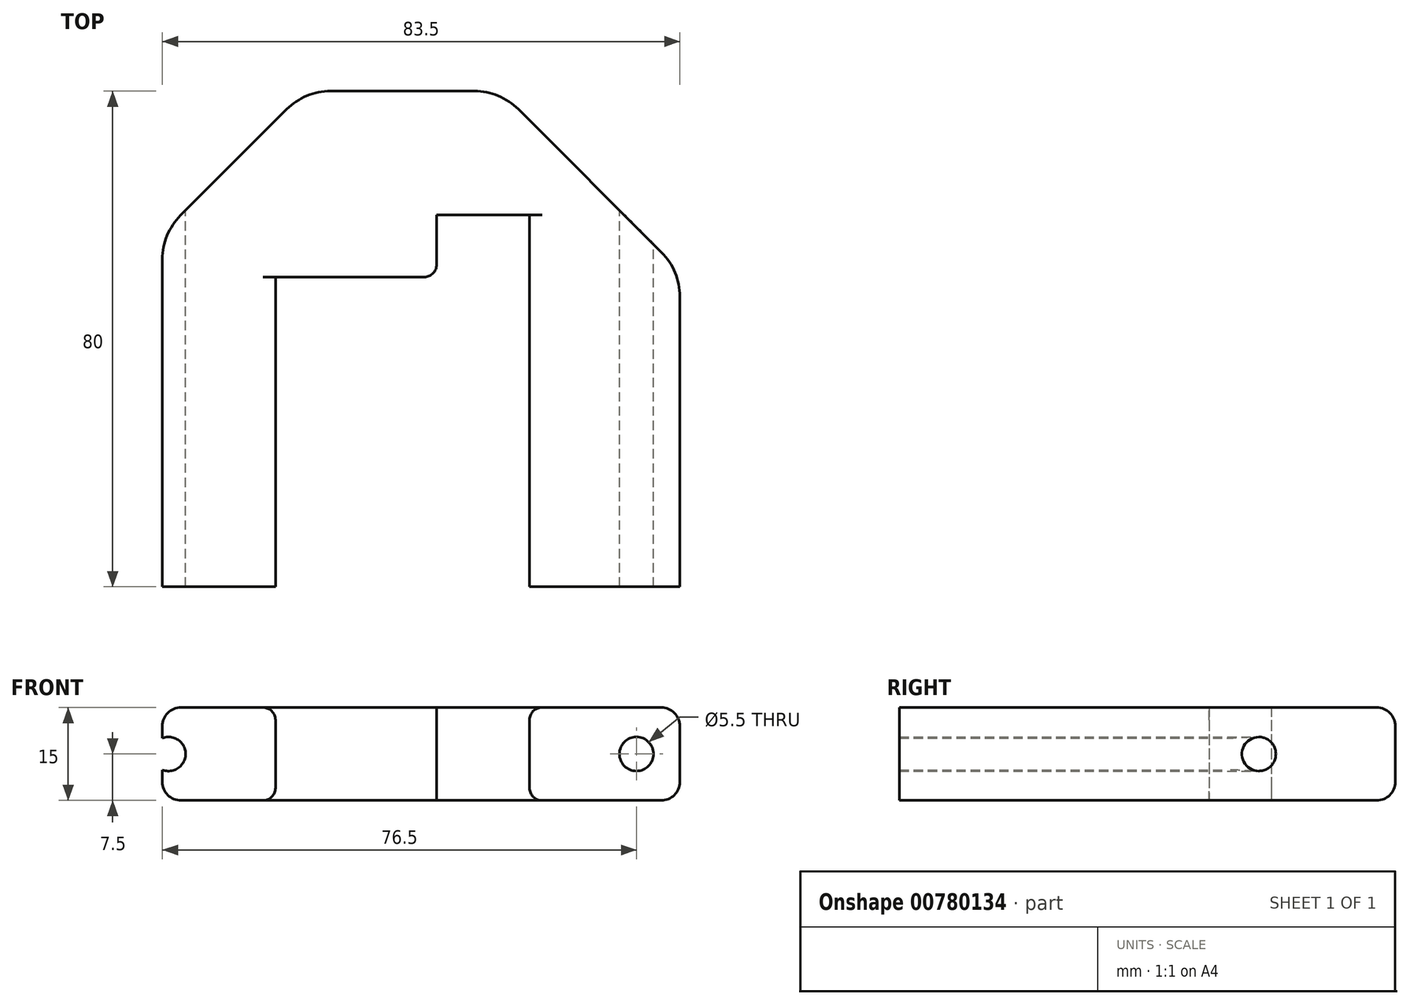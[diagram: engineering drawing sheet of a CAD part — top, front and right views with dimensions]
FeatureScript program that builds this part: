
annotation { "Feature Type Name" : "Feature", "Feature Type Description" : "" }
export const myFeature = defineFeature(function(context is Context, id is Id, definition is map)
    precondition{}
    {
        {
            var Q0;
            Q0=qCreatedBy(makeId("Front.planeOp"),FACE);
            var sketch = newSketch(context, id + "F0", { "sketchPlane" : qUnion([Q0])});
            skLineSegment(sketch, "E0.bottom", {"start": v(-38.75, 15) * mm, "end": v(-20.5, 15) * mm});
            skLineSegment(sketch, "E0.top", {"start": v(-38.75, 0) * mm, "end": v(-20.5, 0) * mm});
            skLineSegment(sketch, "E0.left", {"start": v(-38.75, 15) * mm, "end": v(-38.75, 0) * mm});
            skLineSegment(sketch, "E0.right", {"start": v(-20.5, 15) * mm, "end": v(-20.5, 0) * mm});
            skLineSegment(sketch, "E1", {"start": v(-38.75, 7.5) * mm, "end": v(-37.75, 7.5) * mm});
            skCircle(sketch, "E2", {"center": v(-37.75, 7.5) * mm, "radius": 2.75 * mm});
            skLineSegment(sketch, "E3", {"start": v(0, 35.3) * mm, "end": v(0, -13.85) * mm});
            skLineSegment(sketch, "E4.MirrorCS", {"start": v(38.75, 0) * mm, "end": v(20.5, 0) * mm});
            skLineSegment(sketch, "E5.MirrorCS", {"start": v(38.75, 15) * mm, "end": v(20.5, 15) * mm});
            skLineSegment(sketch, "E6.MirrorCS", {"start": v(38.75, 15) * mm, "end": v(38.75, 0) * mm});
            skCircle(sketch, "E7.MirrorC", {"center": v(37.75, 7.5) * mm, "radius": 2.75 * mm});
            skLineSegment(sketch, "E8.MirrorCS", {"start": v(20.5, 15) * mm, "end": v(20.5, 0) * mm});
            skLineSegment(sketch, "E9.bottom", {"start": v(20.5, 15) * mm, "end": v(5.5, 15) * mm});
            skLineSegment(sketch, "E9.top", {"start": v(20.5, 0) * mm, "end": v(5.5, 0) * mm});
            skLineSegment(sketch, "E9.right", {"start": v(5.5, 15) * mm, "end": v(5.5, 0) * mm});
            skLineSegment(sketch, "E10.bottom", {"start": v(-20.5, 15) * mm, "end": v(5.5, 15) * mm});
            skLineSegment(sketch, "E10.top", {"start": v(-20.5, 15) * mm, "end": v(5.5, 15) * mm});
            skLineSegment(sketch, "E10.left", {"start": v(-20.5, 15) * mm, "end": v(-20.5, 15) * mm});
            skLineSegment(sketch, "E10.right", {"start": v(5.5, 15) * mm, "end": v(5.5, 15) * mm});
            skLineSegment(sketch, "E11.bottom", {"start": v(5.5, 0) * mm, "end": v(-20.5, 0) * mm});
            skLineSegment(sketch, "E11.top", {"start": v(5.5, 0) * mm, "end": v(-20.5, 0) * mm});
            skLineSegment(sketch, "E11.left", {"start": v(5.5, 0) * mm, "end": v(5.5, 0) * mm});
            skLineSegment(sketch, "E11.right", {"start": v(-20.5, 0) * mm, "end": v(-20.5, 0) * mm});
            skLineSegment(sketch, "E12.bottom", {"start": v(38.75, 0) * mm, "end": v(44.75, 0) * mm});
            skLineSegment(sketch, "E12.top", {"start": v(38.75, 15) * mm, "end": v(44.75, 15) * mm});
            skLineSegment(sketch, "E12.left", {"start": v(38.75, 0) * mm, "end": v(38.75, 15) * mm});
            skLineSegment(sketch, "E12.right", {"start": v(44.75, 0) * mm, "end": v(44.75, 15) * mm});
            skSolve(sketch);
        }
        {
            var Q0;
            {var subQ1=sQuery(id+"F0.wireOp",EDGE,"E0.bottom");Q0=makeQuery(id+"F0.imprint","IMPRINT",FACE,{"disambiguationData":[TD([[makeQuery(id+"F0.imprint","IMPRINT",EDGE,{"derivedFrom":subQ1}),-1.0]])]});}
            var Q1;
            {var subQ1=sQuery(id+"F0.wireOp",EDGE,"E4.MirrorCS");Q1=makeQuery(id+"F0.imprint","IMPRINT",FACE,{"disambiguationData":[TD([[makeQuery(id+"F0.imprint","IMPRINT",EDGE,{"derivedFrom":subQ1}),-1.0]])]});}
            var Q2;
            {var subQ1=sQuery(id+"F0.wireOp",EDGE,"E12.bottom");Q2=makeQuery(id+"F0.imprint","IMPRINT",FACE,{"disambiguationData":[TD([[makeQuery(id+"F0.imprint","IMPRINT",EDGE,{"derivedFrom":subQ1}),1.0]])]});}
            extrude(context, id + "F1", {"entities" : qUnion([Q0, Q1, Q2]), "depth" : 80 * mm, "offsetDistance" : 25 * mm});
        }
        {
            var Q0;
            {var subQ0=sQuery(id+"F0.wireOp",EDGE,"E0.right");Q0=makeQuery(id+"F0.imprint","IMPRINT",FACE,{"disambiguationData":[TD([[makeQuery(id+"F0.imprint","IMPRINT",EDGE,{"derivedFrom":subQ0}),1.0]])]});}
            var Q1;
            {var subQ5=sQuery(id+"F0.wireOp",EDGE,"E9.right");Q1=makeQuery(id+"F0.imprint","IMPRINT",FACE,{"disambiguationData":[TD([[makeQuery(id+"F0.imprint","IMPRINT",EDGE,{"derivedFrom":subQ5}),-1.0]])]});}
            extrude(context, id + "F2", {"entities" : qUnion([Q0, Q1]), "operationType" : NewBodyOperationType.ADD, "depth" : 30 * mm, "offsetDistance" : 25 * mm});
        }
        {
            var Q0;
            Q0=makeQuery(id+"F0.imprint","IMPRINT",FACE,{"disambiguationData":[TD([[makeQuery(id+"F0.imprint","IMPRINT",EDGE,{"derivedFrom":sQuery(id+"F0.wireOp",EDGE,"E9.bottom")}),1.0]])]});
            extrude(context, id + "F3", {"entities" : qUnion([Q0]), "operationType" : NewBodyOperationType.ADD, "depth" : 20 * mm, "offsetDistance" : 25 * mm});
        }
        {
            var Q0;
            {var subQ0=sQuery(id+"F0.wireOp",EDGE,"E0.left");Q0=makeQuery(id+"F1.opExtrude","CAP_EDGE",EDGE,{"disambiguationData":[OSD([subQ0]),TDD([makeQuery(id+"F0.imprint","IMPRINT",EDGE,{"disambiguationData":[TD([[makeQuery(id+"F0.imprint","INTERSECT",VERTEX,{"derivedFrom":[sQuery(id+"F0.wireOp",EDGE,"E0.top"),subQ0]}),1.0]])],"derivedFrom":subQ0})])],"isStart":true});}
            var Q1;
            {var subQ0=sQuery(id+"F0.wireOp",EDGE,"E0.left");Q1=makeQuery(id+"F1.opExtrude","CAP_EDGE",EDGE,{"disambiguationData":[OSD([subQ0]),TDD([makeQuery(id+"F0.imprint","IMPRINT",EDGE,{"disambiguationData":[TD([[makeQuery(id+"F0.imprint","INTERSECT",VERTEX,{"derivedFrom":[sQuery(id+"F0.wireOp",EDGE,"E0.bottom"),subQ0]}),-1.0]])],"derivedFrom":subQ0})])],"isStart":true});}
            var Q2;
            {var subQ0=sQuery(id+"F0.wireOp",EDGE,"E6.MirrorCS");Q2=makeQuery(id+"F1.opExtrude","CAP_EDGE",EDGE,{"disambiguationData":[OSD([subQ0]),TDD([makeQuery(id+"F0.imprint","IMPRINT",EDGE,{"disambiguationData":[TD([[makeQuery(id+"F0.imprint","INTERSECT",VERTEX,{"derivedFrom":[sQuery(id+"F0.wireOp",EDGE,"E4.MirrorCS"),subQ0]}),1.0]])],"derivedFrom":subQ0})])],"isStart":true});}
            var Q3;
            {var subQ0=sQuery(id+"F0.wireOp",EDGE,"E6.MirrorCS");Q3=makeQuery(id+"F1.opExtrude","CAP_EDGE",EDGE,{"disambiguationData":[OSD([subQ0]),TDD([makeQuery(id+"F0.imprint","IMPRINT",EDGE,{"disambiguationData":[TD([[makeQuery(id+"F0.imprint","INTERSECT",VERTEX,{"derivedFrom":[sQuery(id+"F0.wireOp",EDGE,"E5.MirrorCS"),subQ0]}),-1.0]])],"derivedFrom":subQ0})])],"isStart":true});}
            chamfer(context, id + "F4", {"entities" : qUnion([Q0, Q1, Q2, Q3]), "width" : 23 * mm, "tangentPropagation" : true});
        }
        {
            var Q0;
            Q0=makeQuery(id+"F1.opExtrude","CAP_EDGE",EDGE,{"disambiguationData":[OSD([sQuery(id+"F0.wireOp",EDGE,"E12.right")])],"isStart":true});
            chamfer(context, id + "F5", {"entities" : qUnion([Q0]), "width" : 29 * mm, "tangentPropagation" : true});
        }
        {
            var Q0;
            {var subQ0=sQuery(id+"F0.wireOp",EDGE,"E9.right");var subQ1=sQuery(id+"F0.wireOp",EDGE,"E8.MirrorCS");var subQ2=sQuery(id+"F0.wireOp",EDGE,"E0.right");var subQ3=sQuery(id+"F0.wireOp",EDGE,"E12.right");Q0=makeQuery(id+"F5.opChamfer","BLEND_EDGE",EDGE,{"blendedFrom":[makeQuery(id+"F1.opExtrude","CAP_EDGE",EDGE,{"disambiguationData":[OSD([subQ3])],"isStart":true}),makeQuery(id+"F3.boolean.opBoolean","MERGE",FACE,{"derivedFrom":[makeQuery(id+"F1.opExtrude","CAP_FACE",FACE,{"disambiguationData":[OSD([sQuery(id+"F0.wireOp",EDGE,"E4.MirrorCS"),sQuery(id+"F0.wireOp",EDGE,"E5.MirrorCS"),sQuery(id+"F0.wireOp",EDGE,"E7.MirrorC"),subQ1,sQuery(id+"F0.wireOp",EDGE,"E12.bottom"),sQuery(id+"F0.wireOp",EDGE,"E12.top"),subQ3])],"isStart":true}),makeQuery(id+"F2.boolean.opBoolean","MERGE",FACE,{"derivedFrom":[makeQuery(id+"F1.opExtrude","CAP_FACE",FACE,{"disambiguationData":[OSD([sQuery(id+"F0.wireOp",EDGE,"E0.bottom"),sQuery(id+"F0.wireOp",EDGE,"E0.top"),sQuery(id+"F0.wireOp",EDGE,"E0.left"),subQ2,sQuery(id+"F0.wireOp",EDGE,"E2")])],"isStart":true}),makeQuery(id+"F2.opExtrude","CAP_FACE",FACE,{"disambiguationData":[OSD([subQ2,subQ0,sQuery(id+"F0.wireOp",EDGE,"E10.top"),sQuery(id+"F0.wireOp",EDGE,"E11.top")])],"isStart":true})]}),makeQuery(id+"F3.opExtrude","CAP_FACE",FACE,{"disambiguationData":[OSD([sQuery(id+"F0.wireOp",EDGE,"E9.bottom"),sQuery(id+"F0.wireOp",EDGE,"E9.top"),subQ1,subQ0])],"isStart":true})]})],"blendedInto":[makeQuery(id+"F3.boolean.opBoolean","MERGE",FACE,{"derivedFrom":[makeQuery(id+"F1.opExtrude","CAP_FACE",FACE,{"disambiguationData":[OSD([sQuery(id+"F0.wireOp",EDGE,"E4.MirrorCS"),sQuery(id+"F0.wireOp",EDGE,"E5.MirrorCS"),sQuery(id+"F0.wireOp",EDGE,"E7.MirrorC"),subQ1,sQuery(id+"F0.wireOp",EDGE,"E12.bottom"),sQuery(id+"F0.wireOp",EDGE,"E12.top"),subQ3])],"isStart":true}),makeQuery(id+"F2.boolean.opBoolean","MERGE",FACE,{"derivedFrom":[makeQuery(id+"F1.opExtrude","CAP_FACE",FACE,{"disambiguationData":[OSD([sQuery(id+"F0.wireOp",EDGE,"E0.bottom"),sQuery(id+"F0.wireOp",EDGE,"E0.top"),sQuery(id+"F0.wireOp",EDGE,"E0.left"),subQ2,sQuery(id+"F0.wireOp",EDGE,"E2")])],"isStart":true}),makeQuery(id+"F2.opExtrude","CAP_FACE",FACE,{"disambiguationData":[OSD([subQ2,subQ0,sQuery(id+"F0.wireOp",EDGE,"E10.top"),sQuery(id+"F0.wireOp",EDGE,"E11.top")])],"isStart":true})]}),makeQuery(id+"F3.opExtrude","CAP_FACE",FACE,{"disambiguationData":[OSD([sQuery(id+"F0.wireOp",EDGE,"E9.bottom"),sQuery(id+"F0.wireOp",EDGE,"E9.top"),subQ1,subQ0])],"isStart":true})]})]});}
            var Q1;
            {var subQ0=sQuery(id+"F0.wireOp",EDGE,"E9.right");var subQ1=sQuery(id+"F0.wireOp",EDGE,"E8.MirrorCS");var subQ2=sQuery(id+"F0.wireOp",EDGE,"E0.right");var subQ3=sQuery(id+"F0.wireOp",EDGE,"E2");var subQ4=sQuery(id+"F0.wireOp",EDGE,"E0.left");var subQ5=sQuery(id+"F0.wireOp",EDGE,"E0.top");Q1=makeQuery(id+"F4.opChamfer","BLEND_EDGE",EDGE,{"blendedFrom":[makeQuery(id+"F1.opExtrude","CAP_EDGE",EDGE,{"disambiguationData":[OSD([subQ4]),TDD([makeQuery(id+"F0.imprint","IMPRINT",EDGE,{"disambiguationData":[TD([[makeQuery(id+"F0.imprint","INTERSECT",VERTEX,{"derivedFrom":[subQ5,subQ4]}),1.0]])],"derivedFrom":subQ4})])],"isStart":true}),makeQuery(id+"F3.boolean.opBoolean","MERGE",FACE,{"derivedFrom":[makeQuery(id+"F1.opExtrude","CAP_FACE",FACE,{"disambiguationData":[OSD([sQuery(id+"F0.wireOp",EDGE,"E4.MirrorCS"),sQuery(id+"F0.wireOp",EDGE,"E5.MirrorCS"),sQuery(id+"F0.wireOp",EDGE,"E7.MirrorC"),subQ1,sQuery(id+"F0.wireOp",EDGE,"E12.bottom"),sQuery(id+"F0.wireOp",EDGE,"E12.top"),sQuery(id+"F0.wireOp",EDGE,"E12.right")])],"isStart":true}),makeQuery(id+"F2.boolean.opBoolean","MERGE",FACE,{"derivedFrom":[makeQuery(id+"F1.opExtrude","CAP_FACE",FACE,{"disambiguationData":[OSD([sQuery(id+"F0.wireOp",EDGE,"E0.bottom"),subQ5,subQ4,subQ2,subQ3])],"isStart":true}),makeQuery(id+"F2.opExtrude","CAP_FACE",FACE,{"disambiguationData":[OSD([subQ2,subQ0,sQuery(id+"F0.wireOp",EDGE,"E10.top"),sQuery(id+"F0.wireOp",EDGE,"E11.top")])],"isStart":true})]}),makeQuery(id+"F3.opExtrude","CAP_FACE",FACE,{"disambiguationData":[OSD([sQuery(id+"F0.wireOp",EDGE,"E9.bottom"),sQuery(id+"F0.wireOp",EDGE,"E9.top"),subQ1,subQ0])],"isStart":true})]})],"blendedInto":[makeQuery(id+"F3.boolean.opBoolean","MERGE",FACE,{"derivedFrom":[makeQuery(id+"F1.opExtrude","CAP_FACE",FACE,{"disambiguationData":[OSD([sQuery(id+"F0.wireOp",EDGE,"E4.MirrorCS"),sQuery(id+"F0.wireOp",EDGE,"E5.MirrorCS"),sQuery(id+"F0.wireOp",EDGE,"E7.MirrorC"),subQ1,sQuery(id+"F0.wireOp",EDGE,"E12.bottom"),sQuery(id+"F0.wireOp",EDGE,"E12.top"),sQuery(id+"F0.wireOp",EDGE,"E12.right")])],"isStart":true}),makeQuery(id+"F2.boolean.opBoolean","MERGE",FACE,{"derivedFrom":[makeQuery(id+"F1.opExtrude","CAP_FACE",FACE,{"disambiguationData":[OSD([sQuery(id+"F0.wireOp",EDGE,"E0.bottom"),subQ5,subQ4,subQ2,subQ3])],"isStart":true}),makeQuery(id+"F2.opExtrude","CAP_FACE",FACE,{"disambiguationData":[OSD([subQ2,subQ0,sQuery(id+"F0.wireOp",EDGE,"E10.top"),sQuery(id+"F0.wireOp",EDGE,"E11.top")])],"isStart":true})]}),makeQuery(id+"F3.opExtrude","CAP_FACE",FACE,{"disambiguationData":[OSD([sQuery(id+"F0.wireOp",EDGE,"E9.bottom"),sQuery(id+"F0.wireOp",EDGE,"E9.top"),subQ1,subQ0])],"isStart":true})]})]});}
            var Q2;
            {var subQ0=sQuery(id+"F0.wireOp",EDGE,"E12.right");Q2=makeQuery(id+"F5.opChamfer","BLEND_EDGE",EDGE,{"blendedFrom":[makeQuery(id+"F1.opExtrude","CAP_EDGE",EDGE,{"disambiguationData":[OSD([subQ0])],"isStart":true}),makeQuery(id+"F1.opExtrude","SWEPT_FACE",FACE,{"disambiguationData":[OSD([subQ0])]})],"blendedInto":[makeQuery(id+"F1.opExtrude","SWEPT_FACE",FACE,{"disambiguationData":[OSD([subQ0])]})]});}
            var Q3;
            {var subQ0=sQuery(id+"F0.wireOp",EDGE,"E0.left");var subQ1=makeQuery(id+"F0.imprint","IMPRINT",EDGE,{"disambiguationData":[TD([[makeQuery(id+"F0.imprint","INTERSECT",VERTEX,{"derivedFrom":[sQuery(id+"F0.wireOp",EDGE,"E0.top"),subQ0]}),1.0]])],"derivedFrom":subQ0});Q3=makeQuery(id+"F4.opChamfer","BLEND_EDGE",EDGE,{"blendedFrom":[makeQuery(id+"F1.opExtrude","CAP_EDGE",EDGE,{"disambiguationData":[OSD([subQ0]),TDD([subQ1])],"isStart":true}),makeQuery(id+"F1.opExtrude","SWEPT_FACE",FACE,{"disambiguationData":[OSD([subQ0]),TDD([subQ1])]})],"blendedInto":[makeQuery(id+"F1.opExtrude","SWEPT_FACE",FACE,{"disambiguationData":[OSD([subQ0]),TDD([subQ1])]})]});}
            var Q4;
            {var subQ0=sQuery(id+"F0.wireOp",EDGE,"E0.left");Q4=makeQuery(id+"F4.opChamfer","BLEND_EDGE",EDGE,{"blendedFrom":[makeQuery(id+"F1.opExtrude","CAP_EDGE",EDGE,{"disambiguationData":[OSD([subQ0]),TDD([makeQuery(id+"F0.imprint","IMPRINT",EDGE,{"disambiguationData":[TD([[makeQuery(id+"F0.imprint","INTERSECT",VERTEX,{"derivedFrom":[sQuery(id+"F0.wireOp",EDGE,"E0.top"),subQ0]}),1.0]])],"derivedFrom":subQ0})])],"isStart":true}),makeQuery(id+"F1.opExtrude","SWEPT_FACE",FACE,{"disambiguationData":[OSD([subQ0]),TDD([makeQuery(id+"F0.imprint","IMPRINT",EDGE,{"disambiguationData":[TD([[makeQuery(id+"F0.imprint","INTERSECT",VERTEX,{"derivedFrom":[sQuery(id+"F0.wireOp",EDGE,"E0.bottom"),subQ0]}),-1.0]])],"derivedFrom":subQ0})])]})],"blendedInto":[makeQuery(id+"F1.opExtrude","SWEPT_FACE",FACE,{"disambiguationData":[OSD([subQ0]),TDD([makeQuery(id+"F0.imprint","IMPRINT",EDGE,{"disambiguationData":[TD([[makeQuery(id+"F0.imprint","INTERSECT",VERTEX,{"derivedFrom":[sQuery(id+"F0.wireOp",EDGE,"E0.bottom"),subQ0]}),-1.0]])],"derivedFrom":subQ0})])]})]});}
            fillet(context, id + "F6", {"entities" : qUnion([Q0, Q1, Q2, Q3, Q4]), "radius" : 10 * mm, "tangentPropagation" : true, "allowEdgeOverflow" : false});
        }
        {
            var Q0;
            Q0=makeQuery(id+"F1.opExtrude","SWEPT_EDGE",EDGE,{"disambiguationData":[OSD([sQuery(id+"F0.wireOp",EDGE,"E5.MirrorCS"),sQuery(id+"F0.wireOp",EDGE,"E9.bottom"),sQuery(id+"F0.wireOp",EDGE,"E8.MirrorCS")])]});
            var Q1;
            Q1=makeQuery(id+"F1.opExtrude","SWEPT_EDGE",EDGE,{"disambiguationData":[OSD([sQuery(id+"F0.wireOp",EDGE,"E4.MirrorCS"),sQuery(id+"F0.wireOp",EDGE,"E9.top"),sQuery(id+"F0.wireOp",EDGE,"E8.MirrorCS")])]});
            var Q2;
            Q2=makeQuery(id+"F1.opExtrude","SWEPT_EDGE",EDGE,{"disambiguationData":[OSD([sQuery(id+"F0.wireOp",EDGE,"E0.bottom"),sQuery(id+"F0.wireOp",EDGE,"E0.right"),sQuery(id+"F0.wireOp",EDGE,"E10.top")])]});
            var Q3;
            Q3=makeQuery(id+"F1.opExtrude","SWEPT_EDGE",EDGE,{"disambiguationData":[OSD([sQuery(id+"F0.wireOp",EDGE,"E0.top"),sQuery(id+"F0.wireOp",EDGE,"E0.right"),sQuery(id+"F0.wireOp",EDGE,"E11.top")])]});
            var Q4;
            Q4=makeQuery(id+"F2.opExtrude","CAP_EDGE",EDGE,{"disambiguationData":[OSD([sQuery(id+"F0.wireOp",EDGE,"E9.right")])],"isStart":false});
            fillet(context, id + "F7", {"entities" : qUnion([Q0, Q1, Q2, Q3, Q4]), "radius" : 2 * mm, "tangentPropagation" : true, "allowEdgeOverflow" : false});
        }
        {
            var Q0;
            Q0=makeQuery(id+"F1.opExtrude","SWEPT_EDGE",EDGE,{"disambiguationData":[OSD([sQuery(id+"F0.wireOp",EDGE,"E0.bottom"),sQuery(id+"F0.wireOp",EDGE,"E0.left")])]});
            var Q1;
            {var subQ0=sQuery(id+"F0.wireOp",EDGE,"E0.bottom");var subQ1=sQuery(id+"F0.wireOp",EDGE,"E0.left");Q1=makeQuery(id+"F6.opFillet","BLEND_EDGE",EDGE,{"blendedFrom":[makeQuery(id+"F4.opChamfer","BLEND_EDGE",EDGE,{"blendedFrom":[makeQuery(id+"F1.opExtrude","CAP_EDGE",EDGE,{"disambiguationData":[OSD([subQ1]),TDD([makeQuery(id+"F0.imprint","IMPRINT",EDGE,{"disambiguationData":[TD([[makeQuery(id+"F0.imprint","INTERSECT",VERTEX,{"derivedFrom":[sQuery(id+"F0.wireOp",EDGE,"E0.top"),subQ1]}),1.0]])],"derivedFrom":subQ1})])],"isStart":true}),makeQuery(id+"F1.opExtrude","SWEPT_FACE",FACE,{"disambiguationData":[OSD([subQ1]),TDD([makeQuery(id+"F0.imprint","IMPRINT",EDGE,{"disambiguationData":[TD([[makeQuery(id+"F0.imprint","INTERSECT",VERTEX,{"derivedFrom":[subQ0,subQ1]}),-1.0]])],"derivedFrom":subQ1})])]})],"blendedInto":[makeQuery(id+"F1.opExtrude","SWEPT_FACE",FACE,{"disambiguationData":[OSD([subQ1]),TDD([makeQuery(id+"F0.imprint","IMPRINT",EDGE,{"disambiguationData":[TD([[makeQuery(id+"F0.imprint","INTERSECT",VERTEX,{"derivedFrom":[subQ0,subQ1]}),-1.0]])],"derivedFrom":subQ1})])]})]}),makeQuery(id+"F3.boolean.opBoolean","MERGE",FACE,{"derivedFrom":[makeQuery(id+"F1.opExtrude","SWEPT_FACE",FACE,{"disambiguationData":[OSD([sQuery(id+"F0.wireOp",EDGE,"E5.MirrorCS"),sQuery(id+"F0.wireOp",EDGE,"E12.top")])]}),makeQuery(id+"F2.boolean.opBoolean","MERGE",FACE,{"derivedFrom":[makeQuery(id+"F1.opExtrude","SWEPT_FACE",FACE,{"disambiguationData":[OSD([subQ0])]}),makeQuery(id+"F2.opExtrude","SWEPT_FACE",FACE,{"disambiguationData":[OSD([sQuery(id+"F0.wireOp",EDGE,"E10.top")])]})]}),makeQuery(id+"F3.opExtrude","SWEPT_FACE",FACE,{"disambiguationData":[OSD([sQuery(id+"F0.wireOp",EDGE,"E9.bottom")])]})]})],"blendedInto":[makeQuery(id+"F3.boolean.opBoolean","MERGE",FACE,{"derivedFrom":[makeQuery(id+"F1.opExtrude","SWEPT_FACE",FACE,{"disambiguationData":[OSD([sQuery(id+"F0.wireOp",EDGE,"E5.MirrorCS"),sQuery(id+"F0.wireOp",EDGE,"E12.top")])]}),makeQuery(id+"F2.boolean.opBoolean","MERGE",FACE,{"derivedFrom":[makeQuery(id+"F1.opExtrude","SWEPT_FACE",FACE,{"disambiguationData":[OSD([subQ0])]}),makeQuery(id+"F2.opExtrude","SWEPT_FACE",FACE,{"disambiguationData":[OSD([sQuery(id+"F0.wireOp",EDGE,"E10.top")])]})]}),makeQuery(id+"F3.opExtrude","SWEPT_FACE",FACE,{"disambiguationData":[OSD([sQuery(id+"F0.wireOp",EDGE,"E9.bottom")])]})]})]});}
            var Q2;
            {var subQ0=sQuery(id+"F0.wireOp",EDGE,"E0.left");Q2=makeQuery(id+"F4.opChamfer","BLEND_EDGE",EDGE,{"blendedFrom":[makeQuery(id+"F1.opExtrude","CAP_EDGE",EDGE,{"disambiguationData":[OSD([subQ0]),TDD([makeQuery(id+"F0.imprint","IMPRINT",EDGE,{"disambiguationData":[TD([[makeQuery(id+"F0.imprint","INTERSECT",VERTEX,{"derivedFrom":[sQuery(id+"F0.wireOp",EDGE,"E0.top"),subQ0]}),1.0]])],"derivedFrom":subQ0})])],"isStart":true}),makeQuery(id+"F3.boolean.opBoolean","MERGE",FACE,{"derivedFrom":[makeQuery(id+"F1.opExtrude","SWEPT_FACE",FACE,{"disambiguationData":[OSD([sQuery(id+"F0.wireOp",EDGE,"E5.MirrorCS"),sQuery(id+"F0.wireOp",EDGE,"E12.top")])]}),makeQuery(id+"F2.boolean.opBoolean","MERGE",FACE,{"derivedFrom":[makeQuery(id+"F1.opExtrude","SWEPT_FACE",FACE,{"disambiguationData":[OSD([sQuery(id+"F0.wireOp",EDGE,"E0.bottom")])]}),makeQuery(id+"F2.opExtrude","SWEPT_FACE",FACE,{"disambiguationData":[OSD([sQuery(id+"F0.wireOp",EDGE,"E10.top")])]})]}),makeQuery(id+"F3.opExtrude","SWEPT_FACE",FACE,{"disambiguationData":[OSD([sQuery(id+"F0.wireOp",EDGE,"E9.bottom")])]})]})],"blendedInto":[makeQuery(id+"F3.boolean.opBoolean","MERGE",FACE,{"derivedFrom":[makeQuery(id+"F1.opExtrude","SWEPT_FACE",FACE,{"disambiguationData":[OSD([sQuery(id+"F0.wireOp",EDGE,"E5.MirrorCS"),sQuery(id+"F0.wireOp",EDGE,"E12.top")])]}),makeQuery(id+"F2.boolean.opBoolean","MERGE",FACE,{"derivedFrom":[makeQuery(id+"F1.opExtrude","SWEPT_FACE",FACE,{"disambiguationData":[OSD([sQuery(id+"F0.wireOp",EDGE,"E0.bottom")])]}),makeQuery(id+"F2.opExtrude","SWEPT_FACE",FACE,{"disambiguationData":[OSD([sQuery(id+"F0.wireOp",EDGE,"E10.top")])]})]}),makeQuery(id+"F3.opExtrude","SWEPT_FACE",FACE,{"disambiguationData":[OSD([sQuery(id+"F0.wireOp",EDGE,"E9.bottom")])]})]})]});}
            var Q3;
            {var subQ0=sQuery(id+"F0.wireOp",EDGE,"E9.bottom");var subQ1=sQuery(id+"F0.wireOp",EDGE,"E10.top");var subQ2=sQuery(id+"F0.wireOp",EDGE,"E0.bottom");var subQ3=sQuery(id+"F0.wireOp",EDGE,"E12.top");var subQ4=sQuery(id+"F0.wireOp",EDGE,"E5.MirrorCS");var subQ5=sQuery(id+"F0.wireOp",EDGE,"E9.right");var subQ6=sQuery(id+"F0.wireOp",EDGE,"E8.MirrorCS");var subQ7=sQuery(id+"F0.wireOp",EDGE,"E0.right");var subQ8=sQuery(id+"F0.wireOp",EDGE,"E2");var subQ9=sQuery(id+"F0.wireOp",EDGE,"E0.left");var subQ10=sQuery(id+"F0.wireOp",EDGE,"E0.top");Q3=makeQuery(id+"F6.opFillet","BLEND_EDGE",EDGE,{"blendedFrom":[makeQuery(id+"F4.opChamfer","BLEND_EDGE",EDGE,{"blendedFrom":[makeQuery(id+"F1.opExtrude","CAP_EDGE",EDGE,{"disambiguationData":[OSD([subQ9]),TDD([makeQuery(id+"F0.imprint","IMPRINT",EDGE,{"disambiguationData":[TD([[makeQuery(id+"F0.imprint","INTERSECT",VERTEX,{"derivedFrom":[subQ10,subQ9]}),1.0]])],"derivedFrom":subQ9})])],"isStart":true}),makeQuery(id+"F3.boolean.opBoolean","MERGE",FACE,{"derivedFrom":[makeQuery(id+"F1.opExtrude","CAP_FACE",FACE,{"disambiguationData":[OSD([sQuery(id+"F0.wireOp",EDGE,"E4.MirrorCS"),subQ4,sQuery(id+"F0.wireOp",EDGE,"E7.MirrorC"),subQ6,sQuery(id+"F0.wireOp",EDGE,"E12.bottom"),subQ3,sQuery(id+"F0.wireOp",EDGE,"E12.right")])],"isStart":true}),makeQuery(id+"F2.boolean.opBoolean","MERGE",FACE,{"derivedFrom":[makeQuery(id+"F1.opExtrude","CAP_FACE",FACE,{"disambiguationData":[OSD([subQ2,subQ10,subQ9,subQ7,subQ8])],"isStart":true}),makeQuery(id+"F2.opExtrude","CAP_FACE",FACE,{"disambiguationData":[OSD([subQ7,subQ5,subQ1,sQuery(id+"F0.wireOp",EDGE,"E11.top")])],"isStart":true})]}),makeQuery(id+"F3.opExtrude","CAP_FACE",FACE,{"disambiguationData":[OSD([subQ0,sQuery(id+"F0.wireOp",EDGE,"E9.top"),subQ6,subQ5])],"isStart":true})]})],"blendedInto":[makeQuery(id+"F3.boolean.opBoolean","MERGE",FACE,{"derivedFrom":[makeQuery(id+"F1.opExtrude","CAP_FACE",FACE,{"disambiguationData":[OSD([sQuery(id+"F0.wireOp",EDGE,"E4.MirrorCS"),subQ4,sQuery(id+"F0.wireOp",EDGE,"E7.MirrorC"),subQ6,sQuery(id+"F0.wireOp",EDGE,"E12.bottom"),subQ3,sQuery(id+"F0.wireOp",EDGE,"E12.right")])],"isStart":true}),makeQuery(id+"F2.boolean.opBoolean","MERGE",FACE,{"derivedFrom":[makeQuery(id+"F1.opExtrude","CAP_FACE",FACE,{"disambiguationData":[OSD([subQ2,subQ10,subQ9,subQ7,subQ8])],"isStart":true}),makeQuery(id+"F2.opExtrude","CAP_FACE",FACE,{"disambiguationData":[OSD([subQ7,subQ5,subQ1,sQuery(id+"F0.wireOp",EDGE,"E11.top")])],"isStart":true})]}),makeQuery(id+"F3.opExtrude","CAP_FACE",FACE,{"disambiguationData":[OSD([subQ0,sQuery(id+"F0.wireOp",EDGE,"E9.top"),subQ6,subQ5])],"isStart":true})]})]}),makeQuery(id+"F3.boolean.opBoolean","MERGE",FACE,{"derivedFrom":[makeQuery(id+"F1.opExtrude","SWEPT_FACE",FACE,{"disambiguationData":[OSD([subQ4,subQ3])]}),makeQuery(id+"F2.boolean.opBoolean","MERGE",FACE,{"derivedFrom":[makeQuery(id+"F1.opExtrude","SWEPT_FACE",FACE,{"disambiguationData":[OSD([subQ2])]}),makeQuery(id+"F2.opExtrude","SWEPT_FACE",FACE,{"disambiguationData":[OSD([subQ1])]})]}),makeQuery(id+"F3.opExtrude","SWEPT_FACE",FACE,{"disambiguationData":[OSD([subQ0])]})]})],"blendedInto":[makeQuery(id+"F3.boolean.opBoolean","MERGE",FACE,{"derivedFrom":[makeQuery(id+"F1.opExtrude","SWEPT_FACE",FACE,{"disambiguationData":[OSD([subQ4,subQ3])]}),makeQuery(id+"F2.boolean.opBoolean","MERGE",FACE,{"derivedFrom":[makeQuery(id+"F1.opExtrude","SWEPT_FACE",FACE,{"disambiguationData":[OSD([subQ2])]}),makeQuery(id+"F2.opExtrude","SWEPT_FACE",FACE,{"disambiguationData":[OSD([subQ1])]})]}),makeQuery(id+"F3.opExtrude","SWEPT_FACE",FACE,{"disambiguationData":[OSD([subQ0])]})]})]});}
            var Q4;
            Q4=makeQuery(id+"F3.boolean.opBoolean","MERGE",EDGE,{"derivedFrom":[makeQuery(id+"F1.opExtrude","CAP_EDGE",EDGE,{"disambiguationData":[OSD([sQuery(id+"F0.wireOp",EDGE,"E5.MirrorCS"),sQuery(id+"F0.wireOp",EDGE,"E12.top")])],"isStart":true}),makeQuery(id+"F2.boolean.opBoolean","MERGE",EDGE,{"derivedFrom":[makeQuery(id+"F1.opExtrude","CAP_EDGE",EDGE,{"disambiguationData":[OSD([sQuery(id+"F0.wireOp",EDGE,"E0.bottom")])],"isStart":true}),makeQuery(id+"F2.opExtrude","CAP_EDGE",EDGE,{"disambiguationData":[OSD([sQuery(id+"F0.wireOp",EDGE,"E10.top")])],"isStart":true})]}),makeQuery(id+"F3.opExtrude","CAP_EDGE",EDGE,{"disambiguationData":[OSD([sQuery(id+"F0.wireOp",EDGE,"E9.bottom")])],"isStart":true})]});
            var Q5;
            {var subQ0=sQuery(id+"F0.wireOp",EDGE,"E9.bottom");var subQ1=sQuery(id+"F0.wireOp",EDGE,"E10.top");var subQ2=sQuery(id+"F0.wireOp",EDGE,"E0.bottom");var subQ3=sQuery(id+"F0.wireOp",EDGE,"E12.top");var subQ4=sQuery(id+"F0.wireOp",EDGE,"E5.MirrorCS");var subQ5=sQuery(id+"F0.wireOp",EDGE,"E9.right");var subQ6=sQuery(id+"F0.wireOp",EDGE,"E8.MirrorCS");var subQ7=sQuery(id+"F0.wireOp",EDGE,"E0.right");var subQ8=sQuery(id+"F0.wireOp",EDGE,"E12.right");Q5=makeQuery(id+"F6.opFillet","BLEND_EDGE",EDGE,{"blendedFrom":[makeQuery(id+"F5.opChamfer","BLEND_EDGE",EDGE,{"blendedFrom":[makeQuery(id+"F1.opExtrude","CAP_EDGE",EDGE,{"disambiguationData":[OSD([subQ8])],"isStart":true}),makeQuery(id+"F3.boolean.opBoolean","MERGE",FACE,{"derivedFrom":[makeQuery(id+"F1.opExtrude","CAP_FACE",FACE,{"disambiguationData":[OSD([sQuery(id+"F0.wireOp",EDGE,"E4.MirrorCS"),subQ4,sQuery(id+"F0.wireOp",EDGE,"E7.MirrorC"),subQ6,sQuery(id+"F0.wireOp",EDGE,"E12.bottom"),subQ3,subQ8])],"isStart":true}),makeQuery(id+"F2.boolean.opBoolean","MERGE",FACE,{"derivedFrom":[makeQuery(id+"F1.opExtrude","CAP_FACE",FACE,{"disambiguationData":[OSD([subQ2,sQuery(id+"F0.wireOp",EDGE,"E0.top"),sQuery(id+"F0.wireOp",EDGE,"E0.left"),subQ7,sQuery(id+"F0.wireOp",EDGE,"E2")])],"isStart":true}),makeQuery(id+"F2.opExtrude","CAP_FACE",FACE,{"disambiguationData":[OSD([subQ7,subQ5,subQ1,sQuery(id+"F0.wireOp",EDGE,"E11.top")])],"isStart":true})]}),makeQuery(id+"F3.opExtrude","CAP_FACE",FACE,{"disambiguationData":[OSD([subQ0,sQuery(id+"F0.wireOp",EDGE,"E9.top"),subQ6,subQ5])],"isStart":true})]})],"blendedInto":[makeQuery(id+"F3.boolean.opBoolean","MERGE",FACE,{"derivedFrom":[makeQuery(id+"F1.opExtrude","CAP_FACE",FACE,{"disambiguationData":[OSD([sQuery(id+"F0.wireOp",EDGE,"E4.MirrorCS"),subQ4,sQuery(id+"F0.wireOp",EDGE,"E7.MirrorC"),subQ6,sQuery(id+"F0.wireOp",EDGE,"E12.bottom"),subQ3,subQ8])],"isStart":true}),makeQuery(id+"F2.boolean.opBoolean","MERGE",FACE,{"derivedFrom":[makeQuery(id+"F1.opExtrude","CAP_FACE",FACE,{"disambiguationData":[OSD([subQ2,sQuery(id+"F0.wireOp",EDGE,"E0.top"),sQuery(id+"F0.wireOp",EDGE,"E0.left"),subQ7,sQuery(id+"F0.wireOp",EDGE,"E2")])],"isStart":true}),makeQuery(id+"F2.opExtrude","CAP_FACE",FACE,{"disambiguationData":[OSD([subQ7,subQ5,subQ1,sQuery(id+"F0.wireOp",EDGE,"E11.top")])],"isStart":true})]}),makeQuery(id+"F3.opExtrude","CAP_FACE",FACE,{"disambiguationData":[OSD([subQ0,sQuery(id+"F0.wireOp",EDGE,"E9.top"),subQ6,subQ5])],"isStart":true})]})]}),makeQuery(id+"F3.boolean.opBoolean","MERGE",FACE,{"derivedFrom":[makeQuery(id+"F1.opExtrude","SWEPT_FACE",FACE,{"disambiguationData":[OSD([subQ4,subQ3])]}),makeQuery(id+"F2.boolean.opBoolean","MERGE",FACE,{"derivedFrom":[makeQuery(id+"F1.opExtrude","SWEPT_FACE",FACE,{"disambiguationData":[OSD([subQ2])]}),makeQuery(id+"F2.opExtrude","SWEPT_FACE",FACE,{"disambiguationData":[OSD([subQ1])]})]}),makeQuery(id+"F3.opExtrude","SWEPT_FACE",FACE,{"disambiguationData":[OSD([subQ0])]})]})],"blendedInto":[makeQuery(id+"F3.boolean.opBoolean","MERGE",FACE,{"derivedFrom":[makeQuery(id+"F1.opExtrude","SWEPT_FACE",FACE,{"disambiguationData":[OSD([subQ4,subQ3])]}),makeQuery(id+"F2.boolean.opBoolean","MERGE",FACE,{"derivedFrom":[makeQuery(id+"F1.opExtrude","SWEPT_FACE",FACE,{"disambiguationData":[OSD([subQ2])]}),makeQuery(id+"F2.opExtrude","SWEPT_FACE",FACE,{"disambiguationData":[OSD([subQ1])]})]}),makeQuery(id+"F3.opExtrude","SWEPT_FACE",FACE,{"disambiguationData":[OSD([subQ0])]})]})]});}
            var Q6;
            Q6=makeQuery(id+"F5.opChamfer","BLEND_EDGE",EDGE,{"blendedFrom":[makeQuery(id+"F1.opExtrude","CAP_EDGE",EDGE,{"disambiguationData":[OSD([sQuery(id+"F0.wireOp",EDGE,"E12.right")])],"isStart":true}),makeQuery(id+"F3.boolean.opBoolean","MERGE",FACE,{"derivedFrom":[makeQuery(id+"F1.opExtrude","SWEPT_FACE",FACE,{"disambiguationData":[OSD([sQuery(id+"F0.wireOp",EDGE,"E5.MirrorCS"),sQuery(id+"F0.wireOp",EDGE,"E12.top")])]}),makeQuery(id+"F2.boolean.opBoolean","MERGE",FACE,{"derivedFrom":[makeQuery(id+"F1.opExtrude","SWEPT_FACE",FACE,{"disambiguationData":[OSD([sQuery(id+"F0.wireOp",EDGE,"E0.bottom")])]}),makeQuery(id+"F2.opExtrude","SWEPT_FACE",FACE,{"disambiguationData":[OSD([sQuery(id+"F0.wireOp",EDGE,"E10.top")])]})]}),makeQuery(id+"F3.opExtrude","SWEPT_FACE",FACE,{"disambiguationData":[OSD([sQuery(id+"F0.wireOp",EDGE,"E9.bottom")])]})]})],"blendedInto":[makeQuery(id+"F3.boolean.opBoolean","MERGE",FACE,{"derivedFrom":[makeQuery(id+"F1.opExtrude","SWEPT_FACE",FACE,{"disambiguationData":[OSD([sQuery(id+"F0.wireOp",EDGE,"E5.MirrorCS"),sQuery(id+"F0.wireOp",EDGE,"E12.top")])]}),makeQuery(id+"F2.boolean.opBoolean","MERGE",FACE,{"derivedFrom":[makeQuery(id+"F1.opExtrude","SWEPT_FACE",FACE,{"disambiguationData":[OSD([sQuery(id+"F0.wireOp",EDGE,"E0.bottom")])]}),makeQuery(id+"F2.opExtrude","SWEPT_FACE",FACE,{"disambiguationData":[OSD([sQuery(id+"F0.wireOp",EDGE,"E10.top")])]})]}),makeQuery(id+"F3.opExtrude","SWEPT_FACE",FACE,{"disambiguationData":[OSD([sQuery(id+"F0.wireOp",EDGE,"E9.bottom")])]})]})]});
            var Q7;
            {var subQ0=sQuery(id+"F0.wireOp",EDGE,"E12.right");Q7=makeQuery(id+"F6.opFillet","BLEND_EDGE",EDGE,{"blendedFrom":[makeQuery(id+"F5.opChamfer","BLEND_EDGE",EDGE,{"blendedFrom":[makeQuery(id+"F1.opExtrude","CAP_EDGE",EDGE,{"disambiguationData":[OSD([subQ0])],"isStart":true}),makeQuery(id+"F1.opExtrude","SWEPT_FACE",FACE,{"disambiguationData":[OSD([subQ0])]})],"blendedInto":[makeQuery(id+"F1.opExtrude","SWEPT_FACE",FACE,{"disambiguationData":[OSD([subQ0])]})]}),makeQuery(id+"F3.boolean.opBoolean","MERGE",FACE,{"derivedFrom":[makeQuery(id+"F1.opExtrude","SWEPT_FACE",FACE,{"disambiguationData":[OSD([sQuery(id+"F0.wireOp",EDGE,"E5.MirrorCS"),sQuery(id+"F0.wireOp",EDGE,"E12.top")])]}),makeQuery(id+"F2.boolean.opBoolean","MERGE",FACE,{"derivedFrom":[makeQuery(id+"F1.opExtrude","SWEPT_FACE",FACE,{"disambiguationData":[OSD([sQuery(id+"F0.wireOp",EDGE,"E0.bottom")])]}),makeQuery(id+"F2.opExtrude","SWEPT_FACE",FACE,{"disambiguationData":[OSD([sQuery(id+"F0.wireOp",EDGE,"E10.top")])]})]}),makeQuery(id+"F3.opExtrude","SWEPT_FACE",FACE,{"disambiguationData":[OSD([sQuery(id+"F0.wireOp",EDGE,"E9.bottom")])]})]})],"blendedInto":[makeQuery(id+"F3.boolean.opBoolean","MERGE",FACE,{"derivedFrom":[makeQuery(id+"F1.opExtrude","SWEPT_FACE",FACE,{"disambiguationData":[OSD([sQuery(id+"F0.wireOp",EDGE,"E5.MirrorCS"),sQuery(id+"F0.wireOp",EDGE,"E12.top")])]}),makeQuery(id+"F2.boolean.opBoolean","MERGE",FACE,{"derivedFrom":[makeQuery(id+"F1.opExtrude","SWEPT_FACE",FACE,{"disambiguationData":[OSD([sQuery(id+"F0.wireOp",EDGE,"E0.bottom")])]}),makeQuery(id+"F2.opExtrude","SWEPT_FACE",FACE,{"disambiguationData":[OSD([sQuery(id+"F0.wireOp",EDGE,"E10.top")])]})]}),makeQuery(id+"F3.opExtrude","SWEPT_FACE",FACE,{"disambiguationData":[OSD([sQuery(id+"F0.wireOp",EDGE,"E9.bottom")])]})]})]});}
            var Q8;
            Q8=makeQuery(id+"F1.opExtrude","SWEPT_EDGE",EDGE,{"disambiguationData":[OSD([sQuery(id+"F0.wireOp",EDGE,"E12.top"),sQuery(id+"F0.wireOp",EDGE,"E12.right")])]});
            var Q9;
            Q9=makeQuery(id+"F1.opExtrude","SWEPT_EDGE",EDGE,{"disambiguationData":[OSD([sQuery(id+"F0.wireOp",EDGE,"E12.bottom"),sQuery(id+"F0.wireOp",EDGE,"E12.right")])]});
            var Q10;
            {var subQ0=sQuery(id+"F0.wireOp",EDGE,"E12.right");Q10=makeQuery(id+"F6.opFillet","BLEND_EDGE",EDGE,{"blendedFrom":[makeQuery(id+"F5.opChamfer","BLEND_EDGE",EDGE,{"blendedFrom":[makeQuery(id+"F1.opExtrude","CAP_EDGE",EDGE,{"disambiguationData":[OSD([subQ0])],"isStart":true}),makeQuery(id+"F1.opExtrude","SWEPT_FACE",FACE,{"disambiguationData":[OSD([subQ0])]})],"blendedInto":[makeQuery(id+"F1.opExtrude","SWEPT_FACE",FACE,{"disambiguationData":[OSD([subQ0])]})]}),makeQuery(id+"F3.boolean.opBoolean","MERGE",FACE,{"derivedFrom":[makeQuery(id+"F1.opExtrude","SWEPT_FACE",FACE,{"disambiguationData":[OSD([sQuery(id+"F0.wireOp",EDGE,"E4.MirrorCS"),sQuery(id+"F0.wireOp",EDGE,"E12.bottom")])]}),makeQuery(id+"F2.boolean.opBoolean","MERGE",FACE,{"derivedFrom":[makeQuery(id+"F1.opExtrude","SWEPT_FACE",FACE,{"disambiguationData":[OSD([sQuery(id+"F0.wireOp",EDGE,"E0.top")])]}),makeQuery(id+"F2.opExtrude","SWEPT_FACE",FACE,{"disambiguationData":[OSD([sQuery(id+"F0.wireOp",EDGE,"E11.top")])]})]}),makeQuery(id+"F3.opExtrude","SWEPT_FACE",FACE,{"disambiguationData":[OSD([sQuery(id+"F0.wireOp",EDGE,"E9.top")])]})]})],"blendedInto":[makeQuery(id+"F3.boolean.opBoolean","MERGE",FACE,{"derivedFrom":[makeQuery(id+"F1.opExtrude","SWEPT_FACE",FACE,{"disambiguationData":[OSD([sQuery(id+"F0.wireOp",EDGE,"E4.MirrorCS"),sQuery(id+"F0.wireOp",EDGE,"E12.bottom")])]}),makeQuery(id+"F2.boolean.opBoolean","MERGE",FACE,{"derivedFrom":[makeQuery(id+"F1.opExtrude","SWEPT_FACE",FACE,{"disambiguationData":[OSD([sQuery(id+"F0.wireOp",EDGE,"E0.top")])]}),makeQuery(id+"F2.opExtrude","SWEPT_FACE",FACE,{"disambiguationData":[OSD([sQuery(id+"F0.wireOp",EDGE,"E11.top")])]})]}),makeQuery(id+"F3.opExtrude","SWEPT_FACE",FACE,{"disambiguationData":[OSD([sQuery(id+"F0.wireOp",EDGE,"E9.top")])]})]})]});}
            fillet(context, id + "F8", {"entities" : qUnion([Q0, Q1, Q2, Q3, Q4, Q5, Q6, Q7, Q8, Q9, Q10]), "radius" : 3 * mm, "tangentPropagation" : true, "allowEdgeOverflow" : false});
        }
    });
